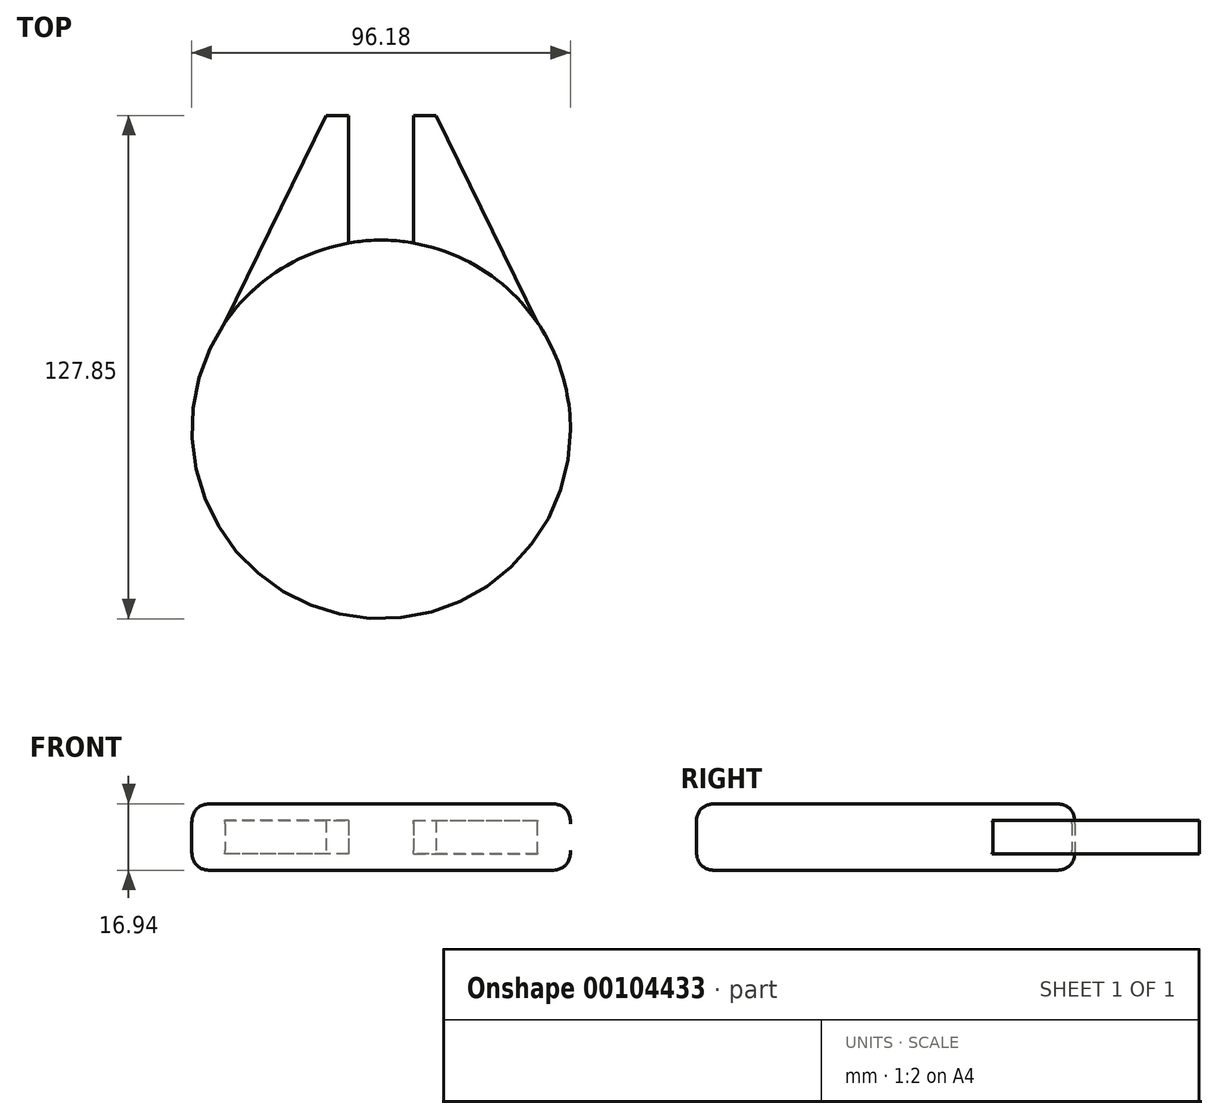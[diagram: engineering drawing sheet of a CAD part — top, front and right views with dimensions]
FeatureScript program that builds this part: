
annotation { "Feature Type Name" : "Feature", "Feature Type Description" : "" }
export const myFeature = defineFeature(function(context is Context, id is Id, definition is map)
    precondition{}
    {
        {
            var Q0;
            Q0=qCreatedBy(makeId("Top.planeOp"),FACE);
            var sketch = newSketch(context, id + "F0", { "sketchPlane" : qUnion([Q0])});
            skLineSegment(sketch, "E0", {"start": v(0, 75.6) * mm, "end": v(0, -70.6) * mm, "construction": true});
            skCircle(sketch, "E1", {"center": v(0, 0) * mm, "radius": 48.1 * mm});
            skLineSegment(sketch, "E2", {"start": v(8.27, 47.38) * mm, "end": v(8.27, 79.76) * mm});
            skLineSegment(sketch, "E3", {"start": v(8.27, 79.76) * mm, "end": v(13.93, 79.76) * mm});
            skLineSegment(sketch, "E4", {"start": v(13.93, 79.76) * mm, "end": v(39.6, 27.28) * mm});
            skLineSegment(sketch, "E5.MirrorCS", {"start": v(-8.27, 47.38) * mm, "end": v(-8.27, 79.76) * mm});
            skLineSegment(sketch, "E6.MirrorCS", {"start": v(-13.93, 79.76) * mm, "end": v(-39.6, 27.28) * mm});
            skLineSegment(sketch, "E7.MirrorCS", {"start": v(-8.27, 79.76) * mm, "end": v(-13.93, 79.76) * mm});
            skSolve(sketch);
        }
        {
            var Q0;
            {var subQ0=sQuery(id+"F0.wireOp",EDGE,"E1");var subQ1=makeQuery(id+"F0.imprint","INTERSECT",VERTEX,{"derivedFrom":[subQ0,sQuery(id+"F0.wireOp",EDGE,"E2")]});Q0=makeQuery(id+"F0.imprint","IMPRINT",FACE,{"disambiguationData":[TD([[makeQuery(id+"F0.imprint","IMPRINT",EDGE,{"disambiguationData":[TD([[subQ1,1.0]])],"derivedFrom":subQ0}),1.0]])]});}
            extrude(context, id + "F1", {"entities" : qUnion([Q0]), "endBound" : BoundingType.SYMMETRIC, "depth" : 16.93 * mm});
        }
        {
            var Q0;
            {var subQ0=sQuery(id+"F0.wireOp",EDGE,"E2");Q0=makeQuery(id+"F0.imprint","IMPRINT",FACE,{"disambiguationData":[TD([[makeQuery(id+"F0.imprint","IMPRINT",EDGE,{"derivedFrom":subQ0}),-1.0]])]});}
            var Q1;
            {var subQ0=sQuery(id+"F0.wireOp",EDGE,"E5.MirrorCS");Q1=makeQuery(id+"F0.imprint","IMPRINT",FACE,{"disambiguationData":[TD([[makeQuery(id+"F0.imprint","IMPRINT",EDGE,{"derivedFrom":subQ0}),1.0]])]});}
            extrude(context, id + "F2", {"entities" : qUnion([Q0, Q1]), "operationType" : NewBodyOperationType.ADD, "endBound" : BoundingType.SYMMETRIC, "depth" : 8.47 * mm});
        }
        {
            var Q0;
            Q0=makeQuery(id+"F1.opExtrude","CAP_EDGE",EDGE,{"disambiguationData":[OSD([sQuery(id+"F0.wireOp",EDGE,"E1")])],"isStart":false});
            var Q1;
            Q1=makeQuery(id+"F1.opExtrude","CAP_EDGE",EDGE,{"disambiguationData":[OSD([sQuery(id+"F0.wireOp",EDGE,"E1")])],"isStart":true});
            fillet(context, id + "F3", {"entities" : qUnion([Q0, Q1]), "radius" : 5.08 * mm, "tangentPropagation" : true, "rho" : 0.5, "crossSection" : FilletCrossSection.CONIC, "allowEdgeOverflow" : false});
        }
    });
